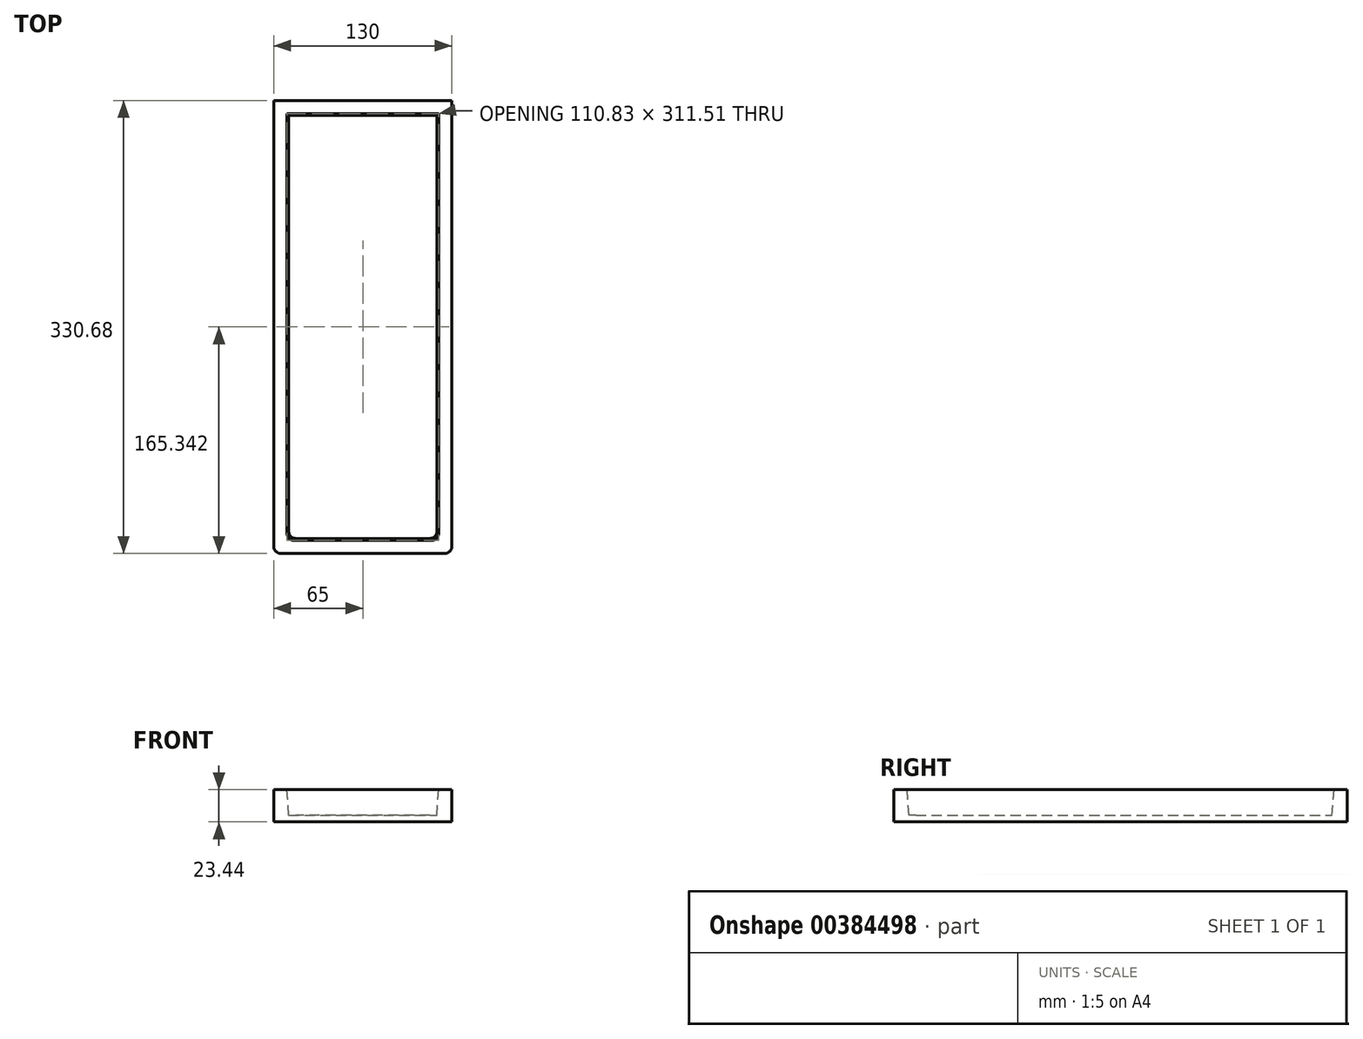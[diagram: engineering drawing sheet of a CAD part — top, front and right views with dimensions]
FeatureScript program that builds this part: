
annotation { "Feature Type Name" : "Feature", "Feature Type Description" : "" }
export const myFeature = defineFeature(function(context is Context, id is Id, definition is map)
    precondition{}
    {
        {
            var Q0;
            Q0=qCreatedBy(makeId("Front.planeOp"),FACE);
            var sketch = newSketch(context, id + "F0", { "sketchPlane" : qUnion([Q0])});
            skLineSegment(sketch, "E0", {"start": v(0, 0) * mm, "end": v(-65, 0) * mm});
            skLineSegment(sketch, "E1", {"start": v(-65, 0) * mm, "end": v(-65, 23.44) * mm});
            skLineSegment(sketch, "E2", {"start": v(-65, 23.44) * mm, "end": v(-55.42, 23.44) * mm});
            skLineSegment(sketch, "E3", {"start": v(-55.42, 23.44) * mm, "end": v(-54.02, 4.8) * mm});
            skLineSegment(sketch, "E4", {"start": v(-54.02, 4.8) * mm, "end": v(0, 4.8) * mm});
            skLineSegment(sketch, "E5", {"start": v(0, 4.8) * mm, "end": v(0, 0) * mm});
            skSolve(sketch);
        }
        {
            var Q0;
            Q0=qCreatedBy(makeId("Top.planeOp"),FACE);
            var sketch = newSketch(context, id + "F1", { "sketchPlane" : qUnion([Q0])});
            skPoint(sketch, "E6.0", {"position": v(-65, 0) * mm});
            skLineSegment(sketch, "E7", {"start": v(-65, 0) * mm, "end": v(-65, 330.68) * mm});
            skLineSegment(sketch, "E8", {"start": v(-65, 330.68) * mm, "end": v(65, 330.68) * mm});
            skLineSegment(sketch, "E9", {"start": v(65, 330.68) * mm, "end": v(65, 0) * mm});
            skLineSegment(sketch, "E10", {"start": v(65, 0) * mm, "end": v(-65, 0) * mm});
            skSolve(sketch);
        }
        {
            var Q0;
            Q0=makeQuery(id+"F0.imprint","IMPRINT",FACE,{"disambiguationData":[TD([[makeQuery(id+"F0.imprint","IMPRINT",EDGE,{"derivedFrom":sQuery(id+"F0.wireOp",EDGE,"E0")}),-1.0]])]});
            var Q1;
            Q1=sQuery(id+"F1.wireOp",EDGE,"E7");
            var Q2;
            Q2=sQuery(id+"F1.wireOp",EDGE,"E8");
            var Q3;
            Q3=sQuery(id+"F1.wireOp",EDGE,"E9");
            var Q4;
            Q4=sQuery(id+"F1.wireOp",EDGE,"E10");
            sweep(context, id + "F2", {"profiles" : qUnion([Q0]), "path" : qUnion([Q1, Q2, Q3, Q4])});
        }
        {
            var Q0;
            Q0=makeQuery(id+"F2.opSweep","MID_CAP_EDGE",EDGE,{"disambiguationData":[OSD([sQuery(id+"F0.wireOp",EDGE,"E1"),sQuery(id+"F1.wireOp",VERTEX,"E10.start")])],"capPos":3.0});
            var Q1;
            Q1=makeQuery(id+"F2.opSweep","CAP_EDGE",EDGE,{"disambiguationData":[OSD([sQuery(id+"F0.wireOp",EDGE,"E1"),sQuery(id+"F1.wireOp",VERTEX,"E10.end")])],"isStart":true});
            fillet(context, id + "F3", {"entities" : qUnion([Q0, Q1]), "radius" : 5 * mm, "tangentPropagation" : true, "allowEdgeOverflow" : false});
        }
        {
            var Q0;
            Q0=makeQuery(id+"F2.opSweep","MID_CAP_EDGE",EDGE,{"disambiguationData":[OSD([sQuery(id+"F0.wireOp",EDGE,"E3"),sQuery(id+"F1.wireOp",VERTEX,"E10.start")])],"capPos":3.0});
            var Q1;
            Q1=makeQuery(id+"F2.opSweep","CAP_EDGE",EDGE,{"disambiguationData":[OSD([sQuery(id+"F0.wireOp",EDGE,"E3"),sQuery(id+"F1.wireOp",VERTEX,"E10.end")])],"isStart":true});
            fillet(context, id + "F4", {"entities" : qUnion([Q0, Q1]), "radius" : 5 * mm, "tangentPropagation" : true, "allowEdgeOverflow" : false});
        }
    });
